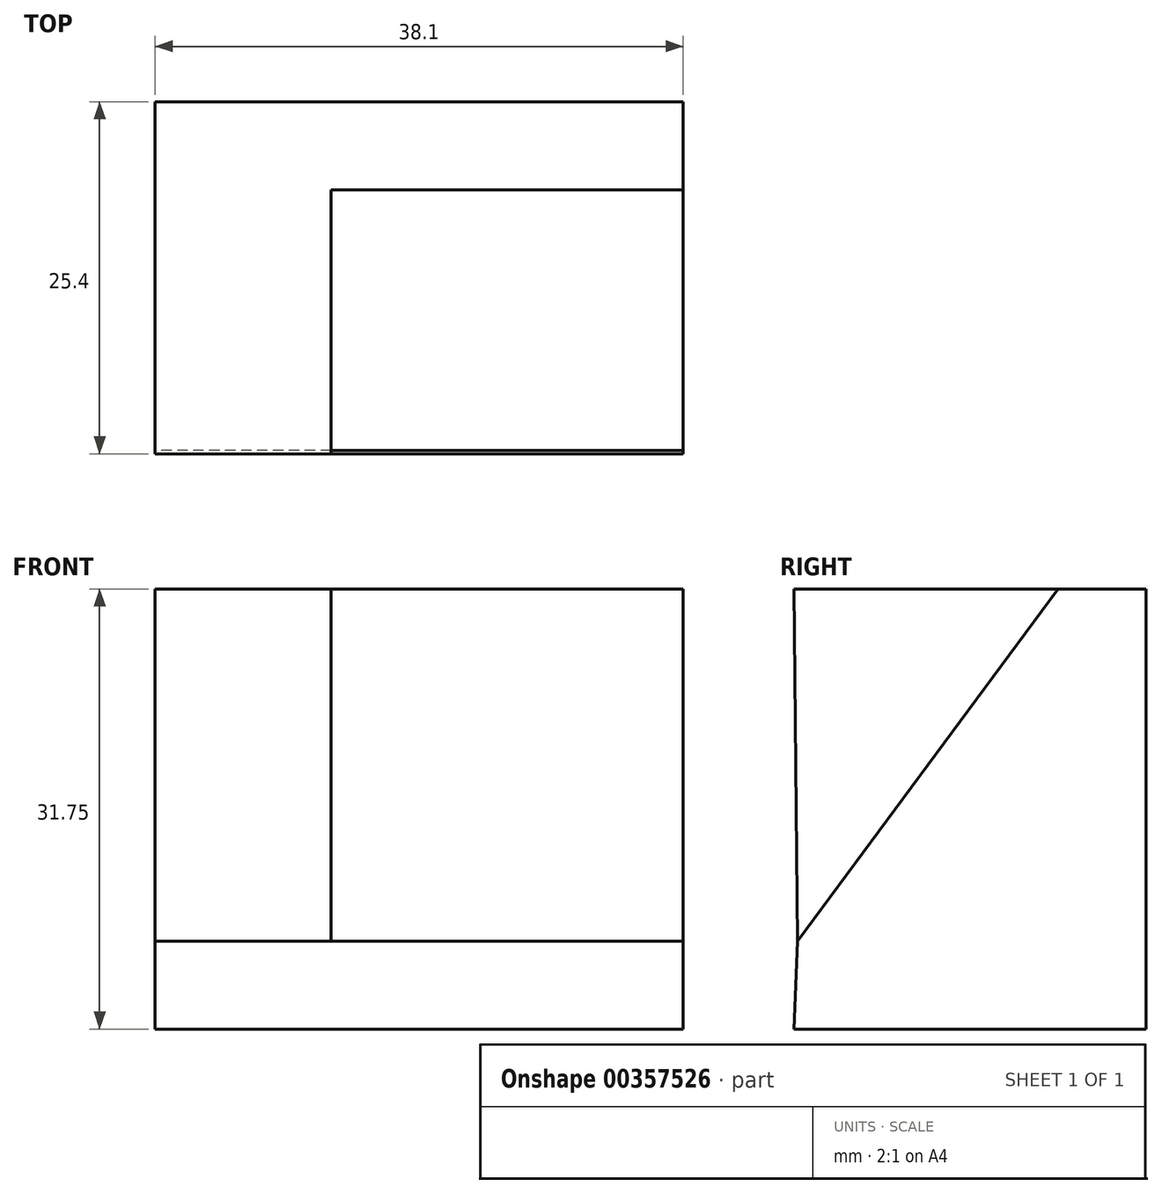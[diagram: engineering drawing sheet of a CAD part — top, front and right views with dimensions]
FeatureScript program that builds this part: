
annotation { "Feature Type Name" : "Feature", "Feature Type Description" : "" }
export const myFeature = defineFeature(function(context is Context, id is Id, definition is map)
    precondition{}
    {
        {
            var Q0;
            Q0=qCreatedBy(makeId("Right.planeOp"),FACE);
            var sketch = newSketch(context, id + "F0", { "sketchPlane" : qUnion([Q0])});
            skLineSegment(sketch, "E0", {"start": v(-54.3, -42.34) * mm, "end": v(-28.9, -42.34) * mm});
            skLineSegment(sketch, "E1", {"start": v(-28.9, -42.34) * mm, "end": v(-28.9, -10.6) * mm});
            skLineSegment(sketch, "E2", {"start": v(-28.9, -10.6) * mm, "end": v(-35.25, -10.6) * mm});
            skLineSegment(sketch, "E3", {"start": v(-35.25, -10.6) * mm, "end": v(-54.05, -36) * mm});
            skLineSegment(sketch, "E4", {"start": v(-54.05, -36) * mm, "end": v(-54.3, -42.34) * mm});
            skLineSegment(sketch, "E5", {"start": v(-35.25, -10.6) * mm, "end": v(-54.3, -10.6) * mm});
            skLineSegment(sketch, "E6", {"start": v(-54.3, -10.6) * mm, "end": v(-54.05, -36) * mm});
            skSolve(sketch);
        }
        {
            var Q0;
            Q0=makeQuery(id+"F0.imprint","IMPRINT",FACE,{"disambiguationData":[TD([[makeQuery(id+"F0.imprint","IMPRINT",EDGE,{"derivedFrom":sQuery(id+"F0.wireOp",EDGE,"E0")}),1.0]])]});
            extrude(context, id + "F1", {"entities" : qUnion([Q0]), "depth" : 38.1 * mm});
        }
        {
            var Q0;
            Q0=makeQuery(id+"F1.opExtrude","CAP_FACE",FACE,{"disambiguationData":[OSD([sQuery(id+"F0.wireOp",EDGE,"E0"),sQuery(id+"F0.wireOp",EDGE,"E1"),sQuery(id+"F0.wireOp",EDGE,"E2"),sQuery(id+"F0.wireOp",EDGE,"E3"),sQuery(id+"F0.wireOp",EDGE,"E4")])],"isStart":true});
            var sketch = newSketch(context, id + "F2", { "sketchPlane" : qUnion([Q0])});
            skLineSegment(sketch, "E7", {"start": v(35.25, -10.6) * mm, "end": v(54.3, -10.6) * mm});
            skLineSegment(sketch, "E8", {"start": v(54.3, -10.6) * mm, "end": v(54.05, -36) * mm});
            skSolve(sketch);
        }
        {
            var Q0;
            Q0=makeQuery(id+"F2.imprint","IMPRINT",FACE,{"disambiguationData":[TD([[makeQuery(id+"F2.imprint","IMPRINT",EDGE,{"derivedFrom":sQuery(id+"F2.wireOp",EDGE,"E7")}),-1.0]])]});
            extrude(context, id + "F3", {"entities" : qUnion([Q0]), "operationType" : NewBodyOperationType.ADD, "oppositeDirection" : true, "depth" : 12.7 * mm});
        }
    });
